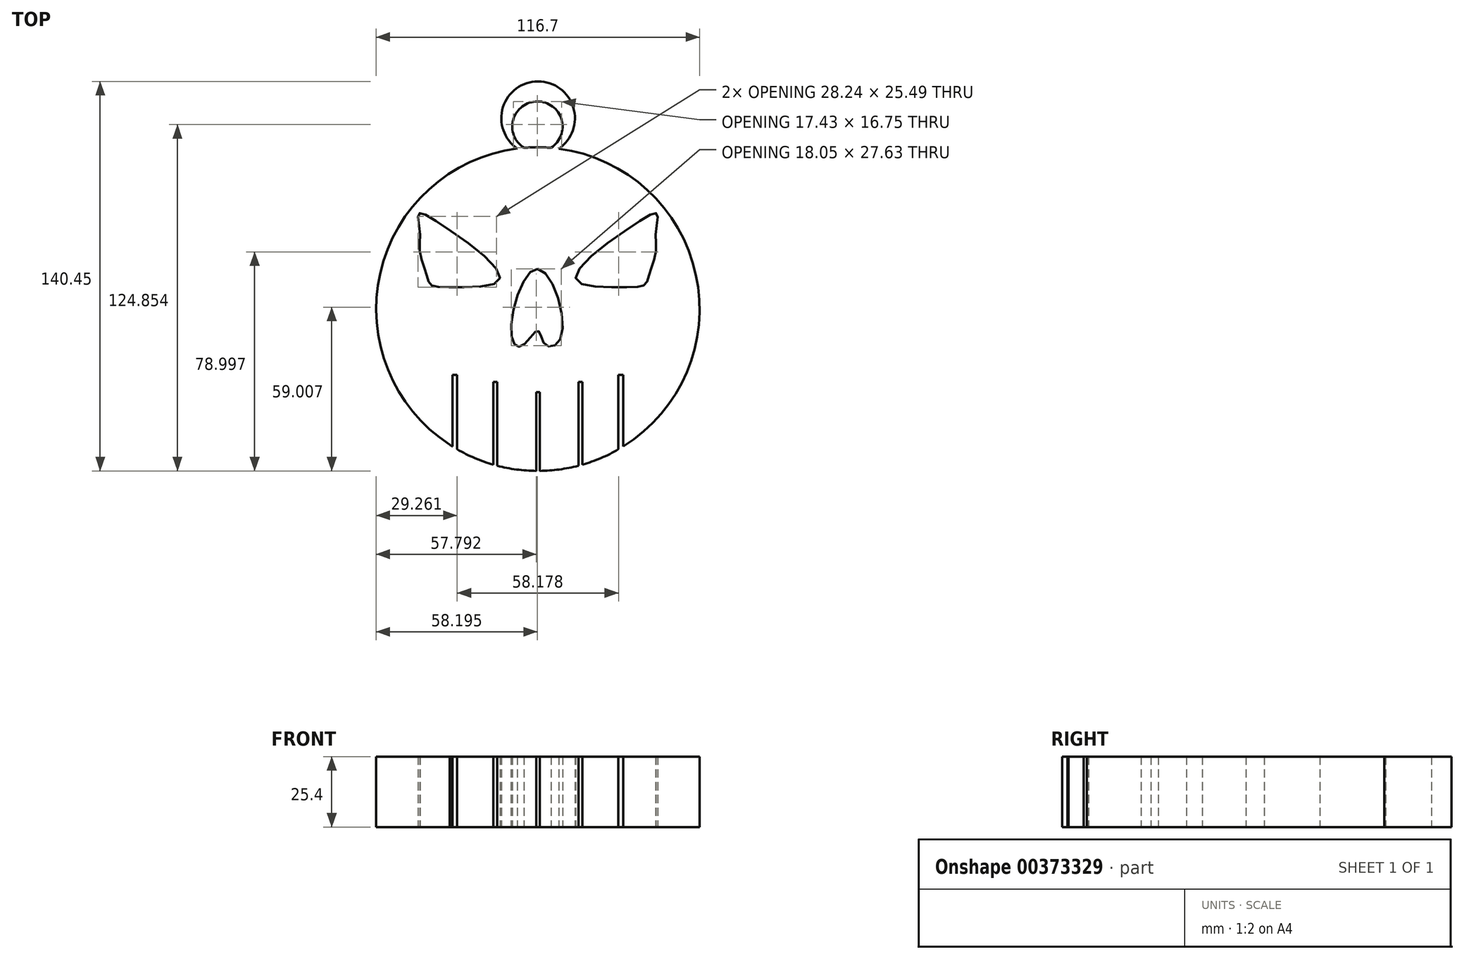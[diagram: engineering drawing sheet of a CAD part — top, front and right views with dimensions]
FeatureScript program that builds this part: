
annotation { "Feature Type Name" : "Feature", "Feature Type Description" : "" }
export const myFeature = defineFeature(function(context is Context, id is Id, definition is map)
    precondition{}
    {
        {
            var Q0;
            Q0=qCreatedBy(makeId("Top.planeOp"),FACE);
            var sketch = newSketch(context, id + "F0", { "sketchPlane" : qUnion([Q0])});
            skCircle(sketch, "E0", {"center": v(0, 45.1) * mm, "radius": 58.35 * mm});
            skLineSegment(sketch, "E1.top", {"start": v(-31.83, -3.8) * mm, "end": v(-31.62, -3.8) * mm});
            skPoint(sketch, "E2.visualSharp", {"position": v(-56.91, 14.33) * mm});
            skPoint(sketch, "E3.visualSharp", {"position": v(57.12, 14.33) * mm});
            skPoint(sketch, "E4.visualSharp", {"position": v(57.12, -3.8) * mm});
            skPoint(sketch, "E5.visualSharp", {"position": v(-56.91, -3.8) * mm});
            skLineSegment(sketch, "E6.right", {"start": v(-31.62, -3.8) * mm, "end": v(-31.62, -3.93) * mm});
            skPoint(sketch, "E6.middle", {"position": v(0.1, -20) * mm});
            skPoint(sketch, "E6.middle.positionSnap0", {"position": v(0.1, -3.8) * mm});
            skPoint(sketch, "E6.centerSnap0", {"position": v(0.1, -3.8) * mm});
            skPoint(sketch, "E7.visualSharp", {"position": v(-31.62, -36.2) * mm});
            skPoint(sketch, "E8.visualSharp", {"position": v(31.83, -36.2) * mm});
            skFitSpline(sketch, "E9", {"points": [v(0, 59.58) * mm, v(-9.61, 36.52) * mm, v(-5.85, 31.76) * mm, v(0, 37.27) * mm, v(2.67, 32.26) * mm, v(8.44, 35.02) * mm, v(0, 59.58) * mm]});
            skFitSpline(sketch, "E10", {"points": [v(36.76, 76.88) * mm, v(13.7, 56.07) * mm, v(32.5, 53.06) * mm, v(38.77, 54.07) * mm, v(40.27, 57.83) * mm, v(42.53, 65.6) * mm, v(42.53, 72.87) * mm, v(43.03, 79.38) * mm, v(36.76, 76.88) * mm]});
            skFitSpline(sketch, "E11.MirrorC", {"points": [v(-36.76, 76.88) * mm, v(-13.7, 56.07) * mm, v(-32.5, 53.06) * mm, v(-38.77, 54.07) * mm, v(-40.27, 57.83) * mm, v(-42.53, 65.6) * mm, v(-42.53, 72.87) * mm, v(-43.03, 79.38) * mm, v(-36.76, 76.88) * mm]});
            skPoint(sketch, "E5.filletArc.end.orphan", {"position": v(-50.56, -3.8) * mm});
            skPoint(sketch, "E12.orphan", {"position": v(50.77, -3.8) * mm});
            skPoint(sketch, "E6.left.start.orphan", {"position": v(31.83, -3.8) * mm});
            skPoint(sketch, "E13.orphan", {"position": v(25.48, -36.2) * mm});
            skPoint(sketch, "E14.top.end.orphan", {"position": v(22.62, -8.68) * mm});
            skPoint(sketch, "E15.bottom.start.orphan", {"position": v(0.1, -36.2) * mm});
            skPoint(sketch, "E7.filletArc.end.orphan", {"position": v(-25.27, -36.2) * mm});
            skPoint(sketch, "E16.top.end.orphan", {"position": v(-22.62, -8.68) * mm});
            skLineSegment(sketch, "E17.bottom", {"start": v(-0.63, -13.24) * mm, "end": v(0.69, -13.24) * mm});
            skLineSegment(sketch, "E17.top", {"start": v(-0.63, 15.2) * mm, "end": v(0.69, 15.2) * mm});
            skLineSegment(sketch, "E17.left", {"start": v(-0.63, -13.24) * mm, "end": v(-0.63, 15.2) * mm});
            skLineSegment(sketch, "E17.right", {"start": v(0.69, -13.24) * mm, "end": v(0.69, 15.2) * mm});
            skLineSegment(sketch, "E18.bottom", {"start": v(14.64, -11.37) * mm, "end": v(16.06, -11.37) * mm});
            skLineSegment(sketch, "E18.top", {"start": v(14.64, 18.78) * mm, "end": v(16.06, 18.78) * mm});
            skLineSegment(sketch, "E18.left", {"start": v(14.64, -11.37) * mm, "end": v(14.64, 18.78) * mm});
            skLineSegment(sketch, "E18.right", {"start": v(16.06, -11.37) * mm, "end": v(16.06, 18.78) * mm});
            skLineSegment(sketch, "E19.MirrorCS", {"start": v(-14.64, -11.37) * mm, "end": v(-14.64, 18.78) * mm});
            skLineSegment(sketch, "E20.MirrorCS", {"start": v(-16.06, -11.37) * mm, "end": v(-16.06, 18.78) * mm});
            skLineSegment(sketch, "E21.MirrorCS", {"start": v(-14.64, 18.78) * mm, "end": v(-16.06, 18.78) * mm});
            skLineSegment(sketch, "E22.MirrorCS", {"start": v(-14.64, -11.37) * mm, "end": v(-16.06, -11.37) * mm});
            skLineSegment(sketch, "E23.bottom", {"start": v(29.09, -5.47) * mm, "end": v(30.85, -5.47) * mm});
            skLineSegment(sketch, "E23.top", {"start": v(29.09, 21.4) * mm, "end": v(30.85, 21.4) * mm});
            skLineSegment(sketch, "E23.left", {"start": v(29.09, -5.47) * mm, "end": v(29.09, 21.4) * mm});
            skLineSegment(sketch, "E23.right", {"start": v(30.85, -5.47) * mm, "end": v(30.85, 21.4) * mm});
            skLineSegment(sketch, "E24.MirrorCS", {"start": v(-29.09, -5.47) * mm, "end": v(-29.09, 21.4) * mm});
            skLineSegment(sketch, "E25.MirrorCS", {"start": v(-30.85, -5.47) * mm, "end": v(-30.85, 21.4) * mm});
            skLineSegment(sketch, "E26.MirrorCS", {"start": v(-29.09, 21.4) * mm, "end": v(-30.85, 21.4) * mm});
            skLineSegment(sketch, "E27.MirrorCS", {"start": v(-29.09, -5.47) * mm, "end": v(-30.85, -5.47) * mm});
            skArc(sketch, "E28", {"start": v(7.57, 102.96) * mm, "mid": v(0.12, 127.21) * mm, "end": v(-7.4, 102.98) * mm});
            skArc(sketch, "E29", {"start": v(4.73, 103.26) * mm, "mid": v(-0.17, 119.99) * mm, "end": v(-5, 103.24) * mm});
            skSolve(sketch);
        }
        {
            var Q0;
            {var subQ18=sQuery(id+"F0.wireOp",EDGE,"E1.top");Q0=makeQuery(id+"F0.imprint","IMPRINT",FACE,{"disambiguationData":[TD([[makeQuery(id+"F0.imprint","IMPRINT",EDGE,{"derivedFrom":subQ18}),1.0]])]});}
            var Q1;
            {var subQ0=sQuery(id+"F0.wireOp",EDGE,"E28");Q1=makeQuery(id+"F0.imprint","IMPRINT",FACE,{"disambiguationData":[TD([[makeQuery(id+"F0.imprint","IMPRINT",EDGE,{"derivedFrom":subQ0}),1.0]])]});}
            extrude(context, id + "F1", {"entities" : qUnion([Q0, Q1]), "depth" : 25.4 * mm});
        }
    });
